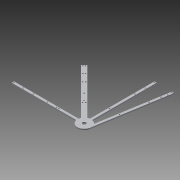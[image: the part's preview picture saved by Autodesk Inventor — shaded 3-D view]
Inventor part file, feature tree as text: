
AUTODESK INVENTOR PART (.ipt)
format: ipt  version: 2013 (Build 170138000, 138)  size: 237,056 bytes
history: native  units: in
note: dims shown in document units (in); Inventor stores cm internally (conversion verified against a paired STEP export)
features: extrude x4, sketch x4, reference x1
ambient origin geometry x8: Origin, YZ Plane, XZ Plane, XY Plane, X Axis, Y Axis, Z Axis, Center Point
feature tree (9):
  extrude  "Extrusion2"  Depth=1.5in
  extrude  "Extrusion8"  Depth=0.25in
  extrude  "Extrusion9"  Depth=2.1762in
  extrude  "Extrusion10"  Depth=0.25in
  sketch  "Sketch1"  dims[d0=0.5in d1=4.0in d2=0.5in d3=0.5in d4=1.5in d5=1.5in d6=1.5in d7=0.25in d8=0.25in d9=0.25in d10=0.5in d11=0.5in d12=3.75in d14=0.266in d15=0.266in d16=0.266in d17=0.25in d18=0.266in d19=0.25in d20=0.25in d21=0.266in d22=0.266in d23=0.266in d24=0.25in d25=0.25in d26=0.266in d28=1.125in d30=0.266in d32=0.266in d33=0.25in d36=1.5in]
  sketch  "Sketch6"  dims[d37=1.0in d38=0.25in]
  sketch  "Sketch8"  dims[d39=5.5in d40=2.1762in]
  sketch  "Sketch9"  dims[d41=5.5in d42=0.25in d43=0.25in d44=0.2874in d45=10.926in d46=10.6389in d47=0.2871in d48=0.2871in d49=15.5in d50=15.5in d51=0.25in d52=0.5in d53=0.266in d54=0.25in d55=0.266in d56=0.266in d57=15.5in d58=0.25in d60=0.266in d61=0.25in d62=0.266in d63=0.266in d64=0.266in d65=0.266in d66=2.0in d67=2.0in d68=2.0in d71=0.297in d72=0.297in d73=0.297in d74=0.297in d75=2.0in d77=0.0in d78=0.25in d79=0.25in d80=0.0in d115=0.266in d117=0.266in d118=9.75in d122=6.0in d123=8.0in d124=0.266in d126=6.0in d127=8.0in d129=0.25in d130=0.25in d131=0.25in d132=0.25in d133=1.0in d134=0.0in d135=0.748in d136=0.25in d137=0.0in d138=1.0in d139=0.0in]
  reference  "Reference1"
